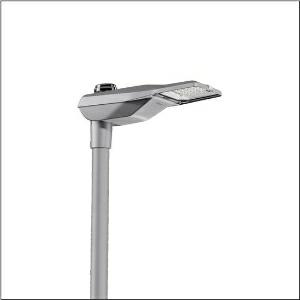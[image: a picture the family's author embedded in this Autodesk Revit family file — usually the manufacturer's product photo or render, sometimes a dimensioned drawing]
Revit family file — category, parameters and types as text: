
# Revit family: streetlight_sl_21_micro___p0_8a_5xe5u47n08cb_fda4
name_source: partatom
category: Lighting Fixtures
units: mm (PartAtom-declared; Revit-internal decimal feet)

## family parameters
Cut with Voids When Loaded = No
Host = Face
Light Source = No
Part Type = Normal
Room Calculation Point = No
Round Connector Dimension = Use Diameter
Shared = No

## types (1)
- --- (1 x LED, 2340 lm, 15.8 W, 4000K)
    Apparent Load = 16 VA
    CIE Flux Codes = 33 69 96 100 100
    Color Rendering = 70
    Color Temperature = 4000K
    Default Elevation = 1800 mm
    Description = Streetlight SL 21 micro, mast luminaire, primary light control with lens, of PMMA, primary optical cover: cover, of toughened safety glass, transparent, light distribution: P0.8a, light emission: direct distribution, primary light characteristic: asymmetric, installation type: post-top, LED, 3G 1.5mm², High Power LED, rated luminous flux: 2.340lm, luminous efficacy: 148lm/W, light colour: 740, colour temperature: 4000K, control gear: NEMA (7pin), control: flexible luminous flux parameterisation, time-dependent luminous flux control, constant luminous flux control, pre-setting: linear dimming characteristic, overheat protection, mains connection: 230..240V, AC, 50/60Hz, connection cable pre-assembled, cable length: 6,5m, wiring characteristics: H07RN-F, start of lifetime: 16W, end of service life: 16W, reduction: 8W, luminaire housing, of diecast aluminium (EN AC-44300), powder-coated, SITECO metallic grey (DB 702S), corrosivity category C5 high according to DIN EN ISO 12944, multi-level sealing system, sealing non-destructively replaceable, inclination adjustable: 0°, 5°, 10°, 15°, length: 528mm, width: 235mm, height: 110mm, spigot size: 76/60mm (post-top), mounting height: 4..8m, protection rating (complete): IP66, insulation class (complete): insulation class I (protective earthing), certification: CE, ENEC, ENEC+, VDE, impact resistance: IK10, permissible operating ambient temperature for outdoor applications: -40..+50°C, standard-compliant lighting for roads and squares, packaging unit: 1 piece

Light Distribution: P0.8a
    Height = 110 mm
    Lamp = 1 x LED
    Lamp Light Flux = 2340 lm
    Lamp Power = 15.8 W
    Lamp count = 1
    Length = 528 mm
    Luminous efficacy = 148 lm/W
    Manufacturer = Siteco
    ModVariant = No
    Model = 5XE5U47N08CB
    Number of Poles = 1
    OnlyDefault = Yes
    Power Factor = 1
    Product Name = Streetlight SL 21 micro | P0.8a
    Product group = mast luminaire | pylon top
    ProductGroupID = 6100
    Protection Class = Protection class I
    Protection Degree = IP 66
    RLX_Detail_Level = 1
    RLX_Emergency_Light_Flux = 0 lm
    RLX_Emergency_Type = 0
    RLX_Emergency_Type_DB = No
    RlxData = <blob elided: 99125 chars, md5=f77f7e43>
    Socket = socket
    Standby Power = 0 W
    System Light Flux = 2340 lm
    System Power = 16 W
    Type Comments = factory setting: luminous flux: 100 % | dim-lin: 254 | 300 mA
    Type Image = l_1294375.jpg
    URL = http://relux.com
    VarID = @adj_081547
    Voltage = 0 V
    Weight = 0.00 kg
    Width = 235 mm

## geometry (parser evidence)
native form markers: Blend x4, Sweep x11
no freeform markers — native parametric forms only
